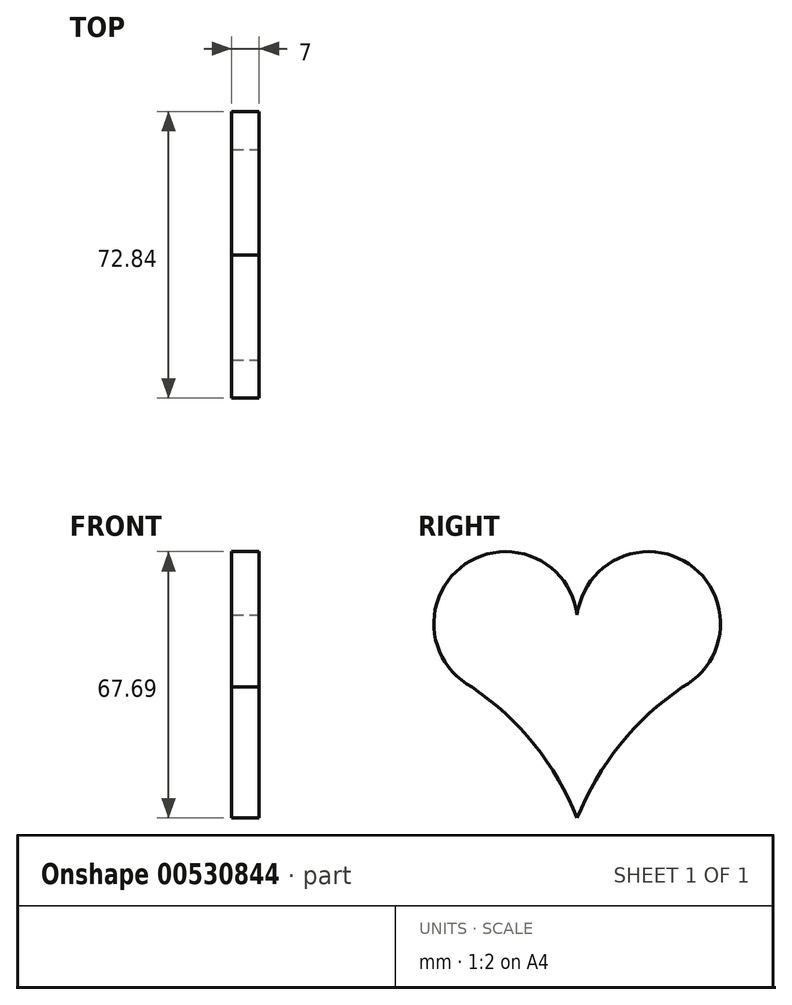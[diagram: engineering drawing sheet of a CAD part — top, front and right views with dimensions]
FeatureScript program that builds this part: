
annotation { "Feature Type Name" : "Feature", "Feature Type Description" : "" }
export const myFeature = defineFeature(function(context is Context, id is Id, definition is map)
    precondition{}
    {
        {
            var Q0;
            Q0=qCreatedBy(makeId("Right.planeOp"),FACE);
            var sketch = newSketch(context, id + "F0", { "sketchPlane" : qUnion([Q0])});
            skArc(sketch, "E0", {"start": v(26.75, 0) * mm, "mid": v(28.45, 31.21) * mm, "end": v(0, 18.26) * mm});
            skArc(sketch, "E1", {"start": v(26.75, 0) * mm, "mid": v(10.88, -14.65) * mm, "end": v(0, -33.3) * mm});
            skArc(sketch, "E2.MirrorCS", {"start": v(-26.75, 0) * mm, "mid": v(-28.45, 31.21) * mm, "end": v(0, 18.26) * mm});
            skArc(sketch, "E3.MirrorCS", {"start": v(-26.75, 0) * mm, "mid": v(-10.88, -14.65) * mm, "end": v(0, -33.3) * mm});
            skPoint(sketch, "E4.orphan", {"position": v(0, -87.32) * mm});
            skSolve(sketch);
        }
        {
            var Q0;
            Q0=makeQuery(id+"F0.imprint","IMPRINT",FACE,{"disambiguationData":[TD([[makeQuery(id+"F0.imprint","IMPRINT",EDGE,{"derivedFrom":sQuery(id+"F0.wireOp",EDGE,"E1")}),-1.0]])]});
            var sketch = newSketch(context, id + "F1", { "sketchPlane" : qUnion([Q0])});
            skSolve(sketch);
        }
        {
            var Q0;
            Q0 = qSketchRegion(id + "F1", true);
            var Q1;
            Q1=makeQuery(id+"F0.imprint","IMPRINT",FACE,{"disambiguationData":[TD([[makeQuery(id+"F0.imprint","IMPRINT",EDGE,{"derivedFrom":sQuery(id+"F0.wireOp",EDGE,"E1")}),-1.0]])]});
            extrude(context, id + "F2", {"entities" : qUnion([Q0, Q1]), "oppositeDirection" : true, "depth" : 7 * mm, "offsetDistance" : 25 * mm});
        }
    });
